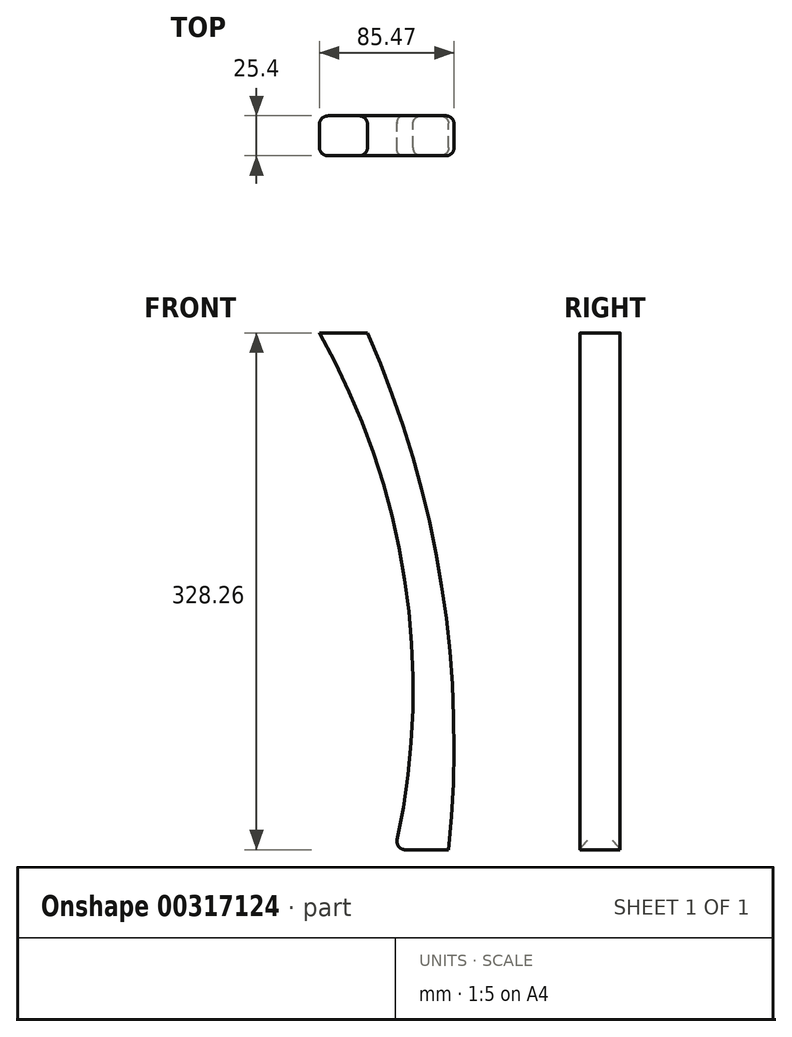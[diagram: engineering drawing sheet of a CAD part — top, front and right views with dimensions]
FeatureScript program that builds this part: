
annotation { "Feature Type Name" : "Feature", "Feature Type Description" : "" }
export const myFeature = defineFeature(function(context is Context, id is Id, definition is map)
    precondition{}
    {
        {
            var Q0;
            Q0=qCreatedBy(makeId("Front.planeOp"),FACE);
            var sketch = newSketch(context, id + "F0", { "sketchPlane" : qUnion([Q0])});
            skArc(sketch, "E0", {"start": v(-13.03, -95.09) * mm, "mid": v(-17.39, 72.4) * mm, "end": v(-64.54, 233.17) * mm});
            skArc(sketch, "E1", {"start": v(-46.96, -95.09) * mm, "mid": v(-40.44, 73.52) * mm, "end": v(-95.02, 233.17) * mm});
            skLineSegment(sketch, "E2", {"start": v(-95.02, 233.17) * mm, "end": v(-64.54, 233.17) * mm});
            skLineSegment(sketch, "E3", {"start": v(-13.03, -95.09) * mm, "end": v(-46.96, -95.09) * mm});
            skSolve(sketch);
        }
        {
            var Q0;
            Q0 = qSketchRegion(id + "F0", true);
            extrude(context, id + "F1", {"entities" : qUnion([Q0]), "depth" : 25.4 * mm});
        }
        {
            var Q0;
            Q0=makeQuery(id+"F1.opExtrude","CAP_EDGE",EDGE,{"disambiguationData":[OSD([sQuery(id+"F0.wireOp",EDGE,"E1")])],"isStart":true});
            var Q1;
            Q1=makeQuery(id+"F1.opExtrude","SWEPT_EDGE",EDGE,{"disambiguationData":[OSD([sQuery(id+"F0.wireOp",EDGE,"E1"),sQuery(id+"F0.wireOp",EDGE,"E3")])]});
            var Q2;
            Q2=makeQuery(id+"F1.opExtrude","CAP_EDGE",EDGE,{"disambiguationData":[OSD([sQuery(id+"F0.wireOp",EDGE,"E0")])],"isStart":false});
            var Q3;
            Q3=makeQuery(id+"F1.opExtrude","CAP_EDGE",EDGE,{"disambiguationData":[OSD([sQuery(id+"F0.wireOp",EDGE,"E1")])],"isStart":false});
            var Q4;
            Q4=makeQuery(id+"F1.opExtrude","CAP_EDGE",EDGE,{"disambiguationData":[OSD([sQuery(id+"F0.wireOp",EDGE,"E0")])],"isStart":true});
            fillet(context, id + "F2", {"entities" : qUnion([Q0, Q1, Q2, Q3, Q4]), "radius" : 5.08 * mm, "tangentPropagation" : true, "allowEdgeOverflow" : false});
        }
    });
